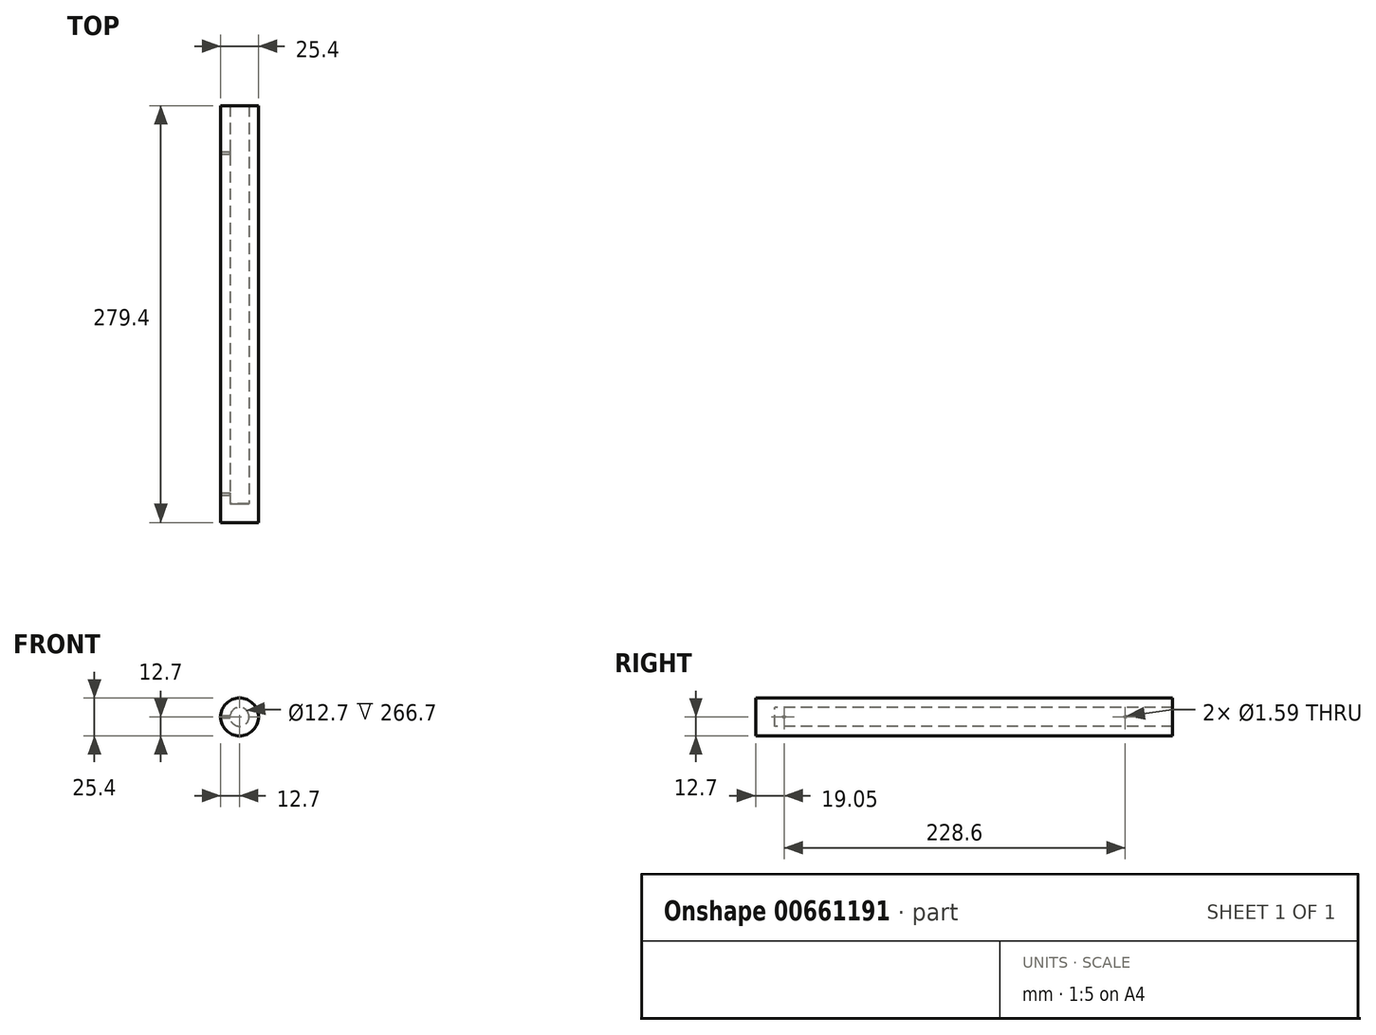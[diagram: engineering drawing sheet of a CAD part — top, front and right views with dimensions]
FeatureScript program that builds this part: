
annotation { "Feature Type Name" : "Feature", "Feature Type Description" : "" }
export const myFeature = defineFeature(function(context is Context, id is Id, definition is map)
    precondition{}
    {
        {
            var Q0;
            Q0=qCreatedBy(makeId("Front.planeOp"),FACE);
            var sketch = newSketch(context, id + "F0", { "sketchPlane" : qUnion([Q0])});
            skCircle(sketch, "E0", {"center": v(0, 0) * mm, "radius": 12.7 * mm});
            skCircle(sketch, "E1", {"center": v(0, 0) * mm, "radius": 6.35 * mm});
            skSolve(sketch);
        }
        {
            var Q0;
            Q0=makeQuery(id+"F0.imprint","IMPRINT",FACE,{"disambiguationData":[TD([[makeQuery(id+"F0.imprint","IMPRINT",EDGE,{"derivedFrom":sQuery(id+"F0.wireOp",EDGE,"E0")}),1.0]])]});
            var Q1;
            Q1=makeQuery(id+"F0.imprint","IMPRINT",FACE,{"disambiguationData":[TD([[makeQuery(id+"F0.imprint","IMPRINT",EDGE,{"derivedFrom":sQuery(id+"F0.wireOp",EDGE,"E1")}),1.0]])]});
            extrude(context, id + "F1", {"entities" : qUnion([Q0, Q1]), "oppositeDirection" : true, "depth" : 12.7 * mm, "offsetDistance" : 25.4 * mm});
        }
        {
            var Q0;
            Q0=makeQuery(id+"F0.imprint","IMPRINT",FACE,{"disambiguationData":[TD([[makeQuery(id+"F0.imprint","IMPRINT",EDGE,{"derivedFrom":sQuery(id+"F0.wireOp",EDGE,"E0")}),1.0]])]});
            extrude(context, id + "F2", {"entities" : qUnion([Q0]), "operationType" : NewBodyOperationType.ADD, "oppositeDirection" : true, "depth" : 279.4 * mm, "offsetDistance" : 25.4 * mm});
        }
        {
            var Q0;
            Q0=makeQuery(id+"F2.opExtrude","CAP_FACE",FACE,{"disambiguationData":[OSD([sQuery(id+"F0.wireOp",EDGE,"E0"),sQuery(id+"F0.wireOp",EDGE,"E1")])],"isStart":false});
            var sketch = newSketch(context, id + "F3", { "sketchPlane" : qUnion([Q0])});
            skCircle(sketch, "E2", {"center": v(0, 0) * mm, "radius": 3.18 * mm});
            skSolve(sketch);
        }
        {
            var Q0;
            Q0=qCreatedBy(makeId("Right.planeOp"),FACE);
            var sketch = newSketch(context, id + "F4", { "sketchPlane" : qUnion([Q0])});
            skLineSegment(sketch, "E3", {"start": v(0, 0) * mm, "end": v(19.05, 0) * mm});
            skCircle(sketch, "E4", {"center": v(19.05, 0) * mm, "radius": 0.8 * mm});
            skSolve(sketch);
        }
        {
            var Q0;
            Q0=makeQuery(id+"F4.imprint","IMPRINT",FACE,{"disambiguationData":[TD([[makeQuery(id+"F4.imprint","IMPRINT",EDGE,{"derivedFrom":sQuery(id+"F4.wireOp",EDGE,"E4")}),1.0]])]});
            var Q1;
            Q1=sQuery(id+"F4.wireOp",EDGE,"E4");
            extrude(context, id + "F5", {"entities" : qUnion([Q0]), "operationType" : NewBodyOperationType.REMOVE, "surfaceEntities" : qUnion([Q1]), "oppositeDirection" : true, "depth" : 25.4 * mm, "offsetDistance" : 25.4 * mm});
        }
        {
            var Q0;
            Q0=qCreatedBy(makeId("Right.planeOp"),FACE);
            var sketch = newSketch(context, id + "F6", { "sketchPlane" : qUnion([Q0])});
            skLineSegment(sketch, "E5", {"start": v(0, 0) * mm, "end": v(247.65, 0) * mm});
            skLineSegment(sketch, "E6", {"start": v(247.65, 0) * mm, "end": v(279.4, 0) * mm});
            skCircle(sketch, "E7", {"center": v(247.65, 0) * mm, "radius": 0.8 * mm});
            skSolve(sketch);
        }
        {
            var Q0;
            {var subQ0=sQuery(id+"F6.wireOp",EDGE,"E6");var subQ1=sQuery(id+"F6.wireOp",EDGE,"E5");var subQ2=makeQuery(id+"F6.imprint","INTERSECT",VERTEX,{"derivedFrom":[subQ1,subQ0]});Q0=makeQuery(id+"F6.imprint","IMPRINT",FACE,{"disambiguationData":[TD([[makeQuery(id+"F6.imprint","IMPRINT",EDGE,{"disambiguationData":[TD([[subQ2,1.0]])],"derivedFrom":subQ1}),1.0]])]});}
            var Q1;
            {var subQ0=sQuery(id+"F6.wireOp",EDGE,"E6");var subQ1=sQuery(id+"F6.wireOp",EDGE,"E5");var subQ2=makeQuery(id+"F6.imprint","INTERSECT",VERTEX,{"derivedFrom":[subQ1,subQ0]});Q1=makeQuery(id+"F6.imprint","IMPRINT",FACE,{"disambiguationData":[TD([[makeQuery(id+"F6.imprint","IMPRINT",EDGE,{"disambiguationData":[TD([[subQ2,1.0]])],"derivedFrom":subQ1}),-1.0]])]});}
            extrude(context, id + "F7", {"entities" : qUnion([Q0, Q1]), "operationType" : NewBodyOperationType.REMOVE, "oppositeDirection" : true, "depth" : 25.4 * mm, "offsetDistance" : 25.4 * mm});
        }
    });
